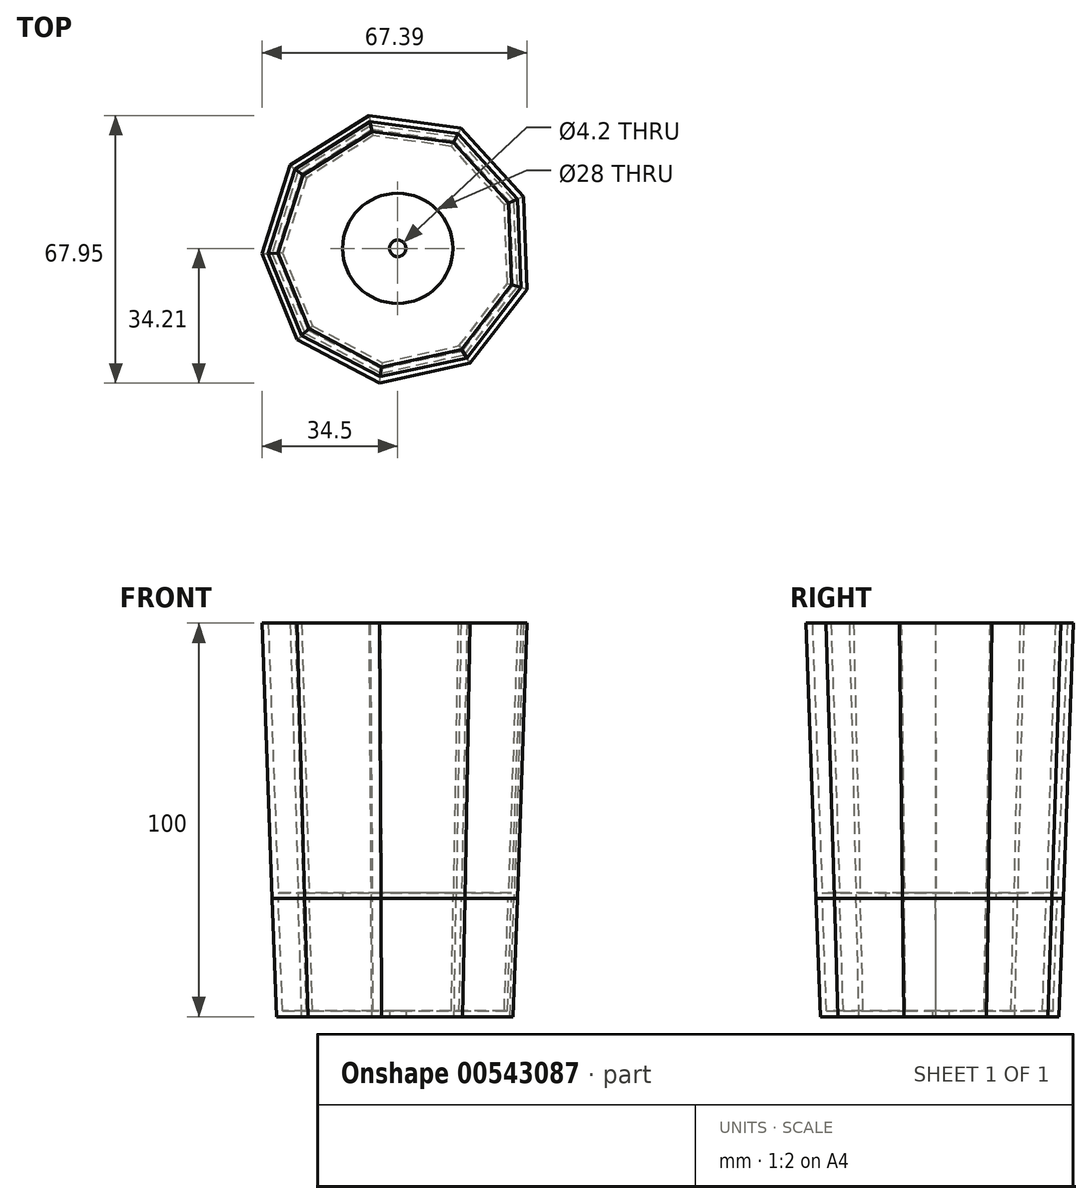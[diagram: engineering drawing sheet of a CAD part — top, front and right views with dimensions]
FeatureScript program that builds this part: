
annotation { "Feature Type Name" : "Feature", "Feature Type Description" : "" }
export const myFeature = defineFeature(function(context is Context, id is Id, definition is map)
    precondition{}
    {
        {
            var Q0;
            Q0=qCreatedBy(makeId("Top.planeOp"),FACE);
            var sketch = newSketch(context, id + "F0", { "sketchPlane" : qUnion([Q0])});
            skCircle(sketch, "E0.cCircle", {"center": v(0, 0) * mm, "radius": 30 * mm, "construction": true});
            skLineSegment(sketch, "E0.0", {"start": v(30.4, -9.72) * mm, "end": v(17.05, -27) * mm});
            skLineSegment(sketch, "E0.1", {"start": v(17.05, -27) * mm, "end": v(-4.3, -31.64) * mm});
            skLineSegment(sketch, "E0.2", {"start": v(-4.3, -31.64) * mm, "end": v(-23.62, -21.48) * mm});
            skLineSegment(sketch, "E0.3", {"start": v(-23.62, -21.48) * mm, "end": v(-31.9, -1.27) * mm});
            skLineSegment(sketch, "E0.4", {"start": v(-31.9, -1.27) * mm, "end": v(-25.25, 19.53) * mm});
            skLineSegment(sketch, "E0.5", {"start": v(-25.25, 19.53) * mm, "end": v(-6.79, 31.2) * mm});
            skLineSegment(sketch, "E0.6", {"start": v(-6.79, 31.2) * mm, "end": v(14.85, 28.26) * mm});
            skLineSegment(sketch, "E0.7", {"start": v(14.85, 28.26) * mm, "end": v(29.54, 12.1) * mm});
            skLineSegment(sketch, "E0.8", {"start": v(29.54, 12.1) * mm, "end": v(30.4, -9.72) * mm});
            skPoint(sketch, "E0.0.midPoint", {"position": v(23.73, -18.36) * mm});
            skSolve(sketch);
        }
        {
            var Q0;
            Q0 = qSketchRegion(id + "F0", true);
            extrude(context, id + "F1", {"entities" : qUnion([Q0]), "depth" : 70 * mm, "offsetDistance" : 25 * mm, "hasDraft" : true, "draftAngle" : 2 * degree});
        }
        {
            var Q0;
            Q0=makeQuery(id+"F1.opExtrude","CAP_FACE",FACE,{"disambiguationData":[OSD([sQuery(id+"F0.wireOp",EDGE,"E0.0"),sQuery(id+"F0.wireOp",EDGE,"E0.1"),sQuery(id+"F0.wireOp",EDGE,"E0.2"),sQuery(id+"F0.wireOp",EDGE,"E0.3"),sQuery(id+"F0.wireOp",EDGE,"E0.4"),sQuery(id+"F0.wireOp",EDGE,"E0.5"),sQuery(id+"F0.wireOp",EDGE,"E0.6"),sQuery(id+"F0.wireOp",EDGE,"E0.7"),sQuery(id+"F0.wireOp",EDGE,"E0.8")])],"isStart":false});
            shell(context, id + "F2", {"entities" : qUnion([Q0]), "thickness" : 1.5 * mm});
        }
        {
            var Q0;
            Q0=makeQuery(id+"F1.opExtrude","CAP_FACE",FACE,{"disambiguationData":[OSD([sQuery(id+"F0.wireOp",EDGE,"E0.0"),sQuery(id+"F0.wireOp",EDGE,"E0.1"),sQuery(id+"F0.wireOp",EDGE,"E0.2"),sQuery(id+"F0.wireOp",EDGE,"E0.3"),sQuery(id+"F0.wireOp",EDGE,"E0.4"),sQuery(id+"F0.wireOp",EDGE,"E0.5"),sQuery(id+"F0.wireOp",EDGE,"E0.6"),sQuery(id+"F0.wireOp",EDGE,"E0.7"),sQuery(id+"F0.wireOp",EDGE,"E0.8")])],"isStart":true});
            var sketch = newSketch(context, id + "F3", { "sketchPlane" : qUnion([Q0])});
            skCircle(sketch, "E1", {"center": v(0, 0) * mm, "radius": 14 * mm});
            skSolve(sketch);
        }
        {
            var Q0;
            Q0 = qSketchRegion(id + "F3", true);
            extrude(context, id + "F4", {"entities" : qUnion([Q0]), "operationType" : NewBodyOperationType.REMOVE, "endBound" : BoundingType.UP_TO_NEXT, "oppositeDirection" : true, "depth" : 25 * mm, "offsetDistance" : 25 * mm});
        }
        {
            var Q0;
            Q0 = qSketchRegion(id + "F0", true);
            var Q1;
            Q1 = qConstructionFilter(qBodyType(qCreatedBy(id + "F0" ,EDGE), BodyType.WIRE), ConstructionObject.NO);
            extrude(context, id + "F5", {"entities" : qUnion([Q0]), "surfaceEntities" : qUnion([Q1]), "oppositeDirection" : true, "depth" : 30 * mm, "offsetDistance" : 25 * mm, "hasDraft" : true, "draftAngle" : 2 * degree, "draftPullDirection" : true});
        }
        {
            var Q0;
            Q0=makeQuery(id+"F5.opExtrude","CAP_FACE",FACE,{"disambiguationData":[OSD([sQuery(id+"F0.wireOp",EDGE,"E0.0"),sQuery(id+"F0.wireOp",EDGE,"E0.1"),sQuery(id+"F0.wireOp",EDGE,"E0.2"),sQuery(id+"F0.wireOp",EDGE,"E0.3"),sQuery(id+"F0.wireOp",EDGE,"E0.4"),sQuery(id+"F0.wireOp",EDGE,"E0.5"),sQuery(id+"F0.wireOp",EDGE,"E0.6"),sQuery(id+"F0.wireOp",EDGE,"E0.7"),sQuery(id+"F0.wireOp",EDGE,"E0.8")])],"isStart":true});
            shell(context, id + "F6", {"entities" : qUnion([Q0]), "thickness" : 1.5 * mm});
        }
        {
            var Q0;
            Q0=makeQuery(id+"F5.opExtrude","CAP_FACE",FACE,{"disambiguationData":[OSD([sQuery(id+"F0.wireOp",EDGE,"E0.0"),sQuery(id+"F0.wireOp",EDGE,"E0.1"),sQuery(id+"F0.wireOp",EDGE,"E0.2"),sQuery(id+"F0.wireOp",EDGE,"E0.3"),sQuery(id+"F0.wireOp",EDGE,"E0.4"),sQuery(id+"F0.wireOp",EDGE,"E0.5"),sQuery(id+"F0.wireOp",EDGE,"E0.6"),sQuery(id+"F0.wireOp",EDGE,"E0.7"),sQuery(id+"F0.wireOp",EDGE,"E0.8")])],"isStart":false});
            var sketch = newSketch(context, id + "F7", { "sketchPlane" : qUnion([Q0])});
            skPoint(sketch, "E2", {"position": v(0, 0) * mm});
            skSolve(sketch);
        }
        {
            var Q0;
            Q0=sQuery(id+"F7.wireOp",VERTEX,"E2");
            var Q1;
            Q1=makeQuery(id+"F5.opExtrude","SWEPT_BODY",BODY,{"disambiguationData":[OSD([sQuery(id+"F0.wireOp",EDGE,"E0.0"),sQuery(id+"F0.wireOp",EDGE,"E0.1"),sQuery(id+"F0.wireOp",EDGE,"E0.2"),sQuery(id+"F0.wireOp",EDGE,"E0.3"),sQuery(id+"F0.wireOp",EDGE,"E0.4"),sQuery(id+"F0.wireOp",EDGE,"E0.5"),sQuery(id+"F0.wireOp",EDGE,"E0.6"),sQuery(id+"F0.wireOp",EDGE,"E0.7"),sQuery(id+"F0.wireOp",EDGE,"E0.8")])]});
            hole(context, id + "F8", {"style" : HoleStyle.SIMPLE, "endStyle" : HoleEndStyle.BLIND, "standardTappedOrClearance" : lookupTablePath({ "standard" : "ISO", "fit" : "Close", "size" : "M4", "type" : "Clearance" }), "standardBlindInLast" : lookupTablePath({ "fit" : "Close", "standard" : "ISO", "size" : "M4", "type" : "Clearance" }), "holeDiameter" : 4.2 * mm, "holeDepth" : 17.25 * mm, "isTappedThrough" : true, "tappedDepth" : 12 * mm, "tapClearance" : 3, "locations" : qUnion([Q0]), "scope" : qUnion([Q1])});
        }
    });
